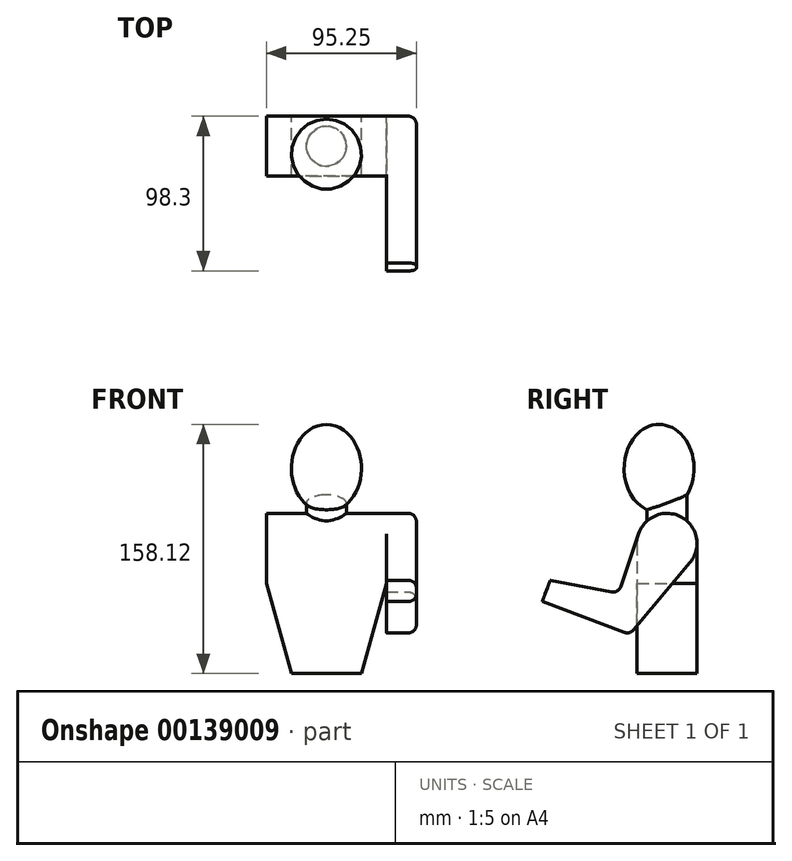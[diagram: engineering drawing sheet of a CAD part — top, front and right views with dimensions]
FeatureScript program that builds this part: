
annotation { "Feature Type Name" : "Feature", "Feature Type Description" : "" }
export const myFeature = defineFeature(function(context is Context, id is Id, definition is map)
    precondition{}
    {
        {
            var Q0;
            Q0=qCreatedBy(makeId("Front.planeOp"),FACE);
            var sketch = newSketch(context, id + "F0", { "sketchPlane" : qUnion([Q0])});
            skLineSegment(sketch, "E0", {"start": v(-22.23, 0) * mm, "end": v(22.23, 0) * mm});
            skLineSegment(sketch, "E1", {"start": v(22.22, 0) * mm, "end": v(38.1, 57.15) * mm});
            skLineSegment(sketch, "E2", {"start": v(38.1, 57.15) * mm, "end": v(38.1, 101.6) * mm});
            skLineSegment(sketch, "E3", {"start": v(38.1, 101.6) * mm, "end": v(-38.1, 101.6) * mm});
            skLineSegment(sketch, "E4", {"start": v(-38.1, 101.6) * mm, "end": v(-38.1, 57.15) * mm});
            skLineSegment(sketch, "E5", {"start": v(-38.1, 57.15) * mm, "end": v(-22.22, 0) * mm});
            skLineSegment(sketch, "E6", {"start": v(0, 0) * mm, "end": v(0, 101.6) * mm, "construction": true});
            skSolve(sketch);
        }
        {
            var Q0;
            Q0 = qSketchRegion(id + "F0", true);
            extrude(context, id + "F1", {"entities" : qUnion([Q0]), "endBound" : BoundingType.SYMMETRIC, "depth" : 38.1 * mm});
        }
        {
            var Q0;
            Q0=makeQuery(id+"F1.opExtrude","CAP_EDGE",EDGE,{"disambiguationData":[OSD([sQuery(id+"F0.wireOp",EDGE,"E3")])],"isStart":false});
            var Q1;
            Q1=makeQuery(id+"F1.opExtrude","CAP_EDGE",EDGE,{"disambiguationData":[OSD([sQuery(id+"F0.wireOp",EDGE,"E3")])],"isStart":true});
            fillet(context, id + "F2", {"entities" : qUnion([Q0, Q1]), "radius" : 19.05 * mm, "tangentPropagation" : true, "allowEdgeOverflow" : false});
        }
        {
            var Q0;
            Q0=qCreatedBy(makeId("Front.planeOp"),FACE);
            var sketch = newSketch(context, id + "F3", { "sketchPlane" : qUnion([Q0])});
            skLineSegment(sketch, "E7.bottom", {"start": v(0, 82.55) * mm, "end": v(12.7, 82.55) * mm});
            skLineSegment(sketch, "E7.top", {"start": v(0, 120.65) * mm, "end": v(12.7, 120.65) * mm});
            skLineSegment(sketch, "E7.left", {"start": v(0, 82.55) * mm, "end": v(0, 120.65) * mm});
            skLineSegment(sketch, "E7.right", {"start": v(12.7, 82.55) * mm, "end": v(12.7, 120.65) * mm});
            skLineSegment(sketch, "E8", {"start": v(0, 82.55) * mm, "end": v(0, 0) * mm, "construction": true});
            skSolve(sketch);
        }
        {
            var Q0;
            Q0 = qSketchRegion(id + "F3", true);
            var Q1;
            Q1=sQuery(id+"F3.wireOp",EDGE,"E8");
            revolve(context, id + "F4", {"operationType" : NewBodyOperationType.ADD, "entities" : qUnion([Q0]), "axis" : qUnion([Q1]), "revolveType" : RevolveType.FULL});
        }
        {
            var Q0;
            Q0=qCreatedBy(makeId("Right.planeOp"),FACE);
            var sketch = newSketch(context, id + "F5", { "sketchPlane" : qUnion([Q0])});
            skLineSegment(sketch, "E9", {"start": v(-5.08, 102.24) * mm, "end": v(-5.08, 158.12) * mm});
            skEllipticalArc(sketch, "E10", {});
            skLineSegment(sketch, "E11", {"start": v(-5.08, 102.24) * mm, "end": v(-5.08, 8.32) * mm, "construction": true});
            skLineSegment(sketch, "E12", {"start": v(-5.08, 130.18) * mm, "end": v(17.14, 130.18) * mm, "construction": true});
            const initialGuessF5  = {"E10": [-0.00508, 0.130175, 0, 1, 0.02794, 0.022225, 3.141592653589793, 0]};
            skSetInitialGuess(sketch, initialGuessF5);
            skSolve(sketch);
        }
        {
            var Q0;
            Q0 = qSketchRegion(id + "F5", true);
            var Q1;
            Q1=sQuery(id+"F5.wireOp",EDGE,"E11");
            revolve(context, id + "F6", {"operationType" : NewBodyOperationType.ADD, "entities" : qUnion([Q0]), "axis" : qUnion([Q1]), "revolveType" : RevolveType.FULL});
        }
        {
            var Q0;
            Q0=makeQuery(id+"F1.opExtrude","SWEPT_FACE",FACE,{"disambiguationData":[OSD([sQuery(id+"F0.wireOp",EDGE,"E2")])]});
            var sketch = newSketch(context, id + "F7", { "sketchPlane" : qUnion([Q0])});
            skArc(sketch, "E13", {"start": v(14.6, 70.3) * mm, "mid": v(9.35, 99.15) * mm, "end": v(-18.04, 88.68) * mm});
            skLineSegment(sketch, "E14", {"start": v(14.6, 70.3) * mm, "end": v(-23.62, 24.76) * mm});
            skLineSegment(sketch, "E15", {"start": v(-23.62, 24.76) * mm, "end": v(-79.25, 45.66) * mm});
            skLineSegment(sketch, "E16", {"start": v(-79.25, 45.66) * mm, "end": v(-74.21, 59.06) * mm});
            skLineSegment(sketch, "E17", {"start": v(-74.21, 59.06) * mm, "end": v(-30.86, 50.96) * mm});
            skLineSegment(sketch, "E18", {"start": v(-30.86, 50.96) * mm, "end": v(-18.04, 88.68) * mm});
            skSolve(sketch);
        }
        {
            var Q0;
            Q0 = qSketchRegion(id + "F7", true);
            extrude(context, id + "F8", {"entities" : qUnion([Q0]), "operationType" : NewBodyOperationType.ADD, "depth" : 19.05 * mm});
        }
        {
            var Q0;
            Q0=makeQuery(id+"F8.opExtrude","SWEPT_EDGE",EDGE,{"disambiguationData":[OSD([sQuery(id+"F7.wireOp",EDGE,"E17"),sQuery(id+"F7.wireOp",EDGE,"E18")])]});
            fillet(context, id + "F9", {"entities" : qUnion([Q0]), "radius" : 5.08 * mm, "tangentPropagation" : true, "allowEdgeOverflow" : false});
        }
        {
            var Q0;
            Q0=makeQuery(id+"F8.opExtrude","SWEPT_EDGE",EDGE,{"disambiguationData":[OSD([sQuery(id+"F7.wireOp",EDGE,"E14"),sQuery(id+"F7.wireOp",EDGE,"E15")])]});
            fillet(context, id + "F10", {"entities" : qUnion([Q0]), "radius" : 5.08 * mm, "tangentPropagation" : true, "allowEdgeOverflow" : false});
        }
        {
            var Q0;
            Q0=makeQuery(id+"F8.opExtrude","CAP_EDGE",EDGE,{"disambiguationData":[OSD([sQuery(id+"F7.wireOp",EDGE,"E14")])],"isStart":false});
            fillet(context, id + "F11", {"entities" : qUnion([Q0]), "radius" : 5.08 * mm, "tangentPropagation" : true, "allowEdgeOverflow" : false});
        }
    });
